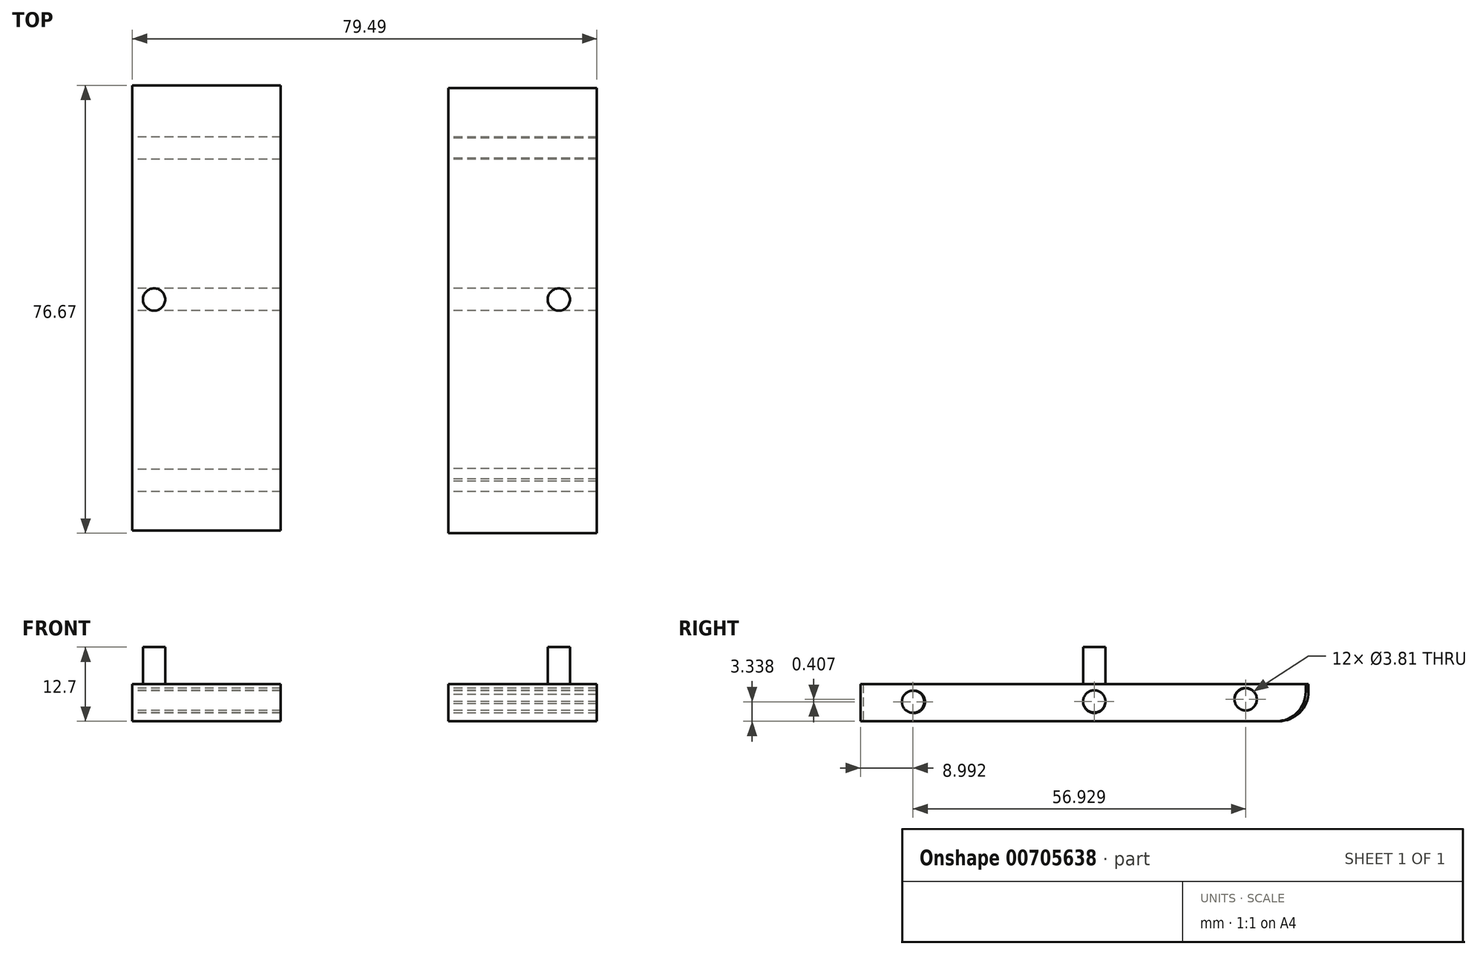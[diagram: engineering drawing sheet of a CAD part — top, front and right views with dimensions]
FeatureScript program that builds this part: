
annotation { "Feature Type Name" : "Feature", "Feature Type Description" : "" }
export const myFeature = defineFeature(function(context is Context, id is Id, definition is map)
    precondition{}
    {
        {
            var Q0;
            Q0=qCreatedBy(makeId("Top.planeOp"),FACE);
            var sketch = newSketch(context, id + "F0", { "sketchPlane" : qUnion([Q0])});
            skLineSegment(sketch, "E0.bottom", {"start": v(-44.7, 36.67) * mm, "end": v(-19.3, 36.67) * mm});
            skLineSegment(sketch, "E0.top", {"start": v(-44.7, -39.53) * mm, "end": v(-19.3, -39.53) * mm});
            skLineSegment(sketch, "E0.left", {"start": v(-44.7, 36.67) * mm, "end": v(-44.7, -39.53) * mm});
            skLineSegment(sketch, "E0.right", {"start": v(-19.3, 36.67) * mm, "end": v(-19.3, -39.53) * mm});
            skLineSegment(sketch, "E1.bottom", {"start": v(9.39, 36.2) * mm, "end": v(34.79, 36.2) * mm});
            skLineSegment(sketch, "E1.top", {"start": v(9.39, -40) * mm, "end": v(34.79, -40) * mm});
            skLineSegment(sketch, "E1.left", {"start": v(9.39, 36.2) * mm, "end": v(9.39, -40) * mm});
            skLineSegment(sketch, "E1.right", {"start": v(34.79, 36.2) * mm, "end": v(34.79, -40) * mm});
            skSolve(sketch);
        }
        {
            var Q0;
            Q0=makeQuery(id+"F0.imprint","IMPRINT",FACE,{"disambiguationData":[TD([[makeQuery(id+"F0.imprint","IMPRINT",EDGE,{"derivedFrom":sQuery(id+"F0.wireOp",EDGE,"E0.bottom")}),-1.0]])]});
            var Q1;
            Q1=makeQuery(id+"F0.imprint","IMPRINT",FACE,{"disambiguationData":[TD([[makeQuery(id+"F0.imprint","IMPRINT",EDGE,{"derivedFrom":sQuery(id+"F0.wireOp",EDGE,"E1.bottom")}),-1.0]])]});
            extrude(context, id + "F1", {"entities" : qUnion([Q0, Q1]), "depth" : 6.35 * mm, "offsetDistance" : 25.4 * mm});
        }
        {
            var Q0;
            Q0=makeQuery(id+"F1.opExtrude","CAP_EDGE",EDGE,{"disambiguationData":[OSD([sQuery(id+"F0.wireOp",EDGE,"E0.bottom")])],"isStart":true});
            var Q1;
            Q1=makeQuery(id+"F1.opExtrude","CAP_EDGE",EDGE,{"disambiguationData":[OSD([sQuery(id+"F0.wireOp",EDGE,"E1.bottom")])],"isStart":true});
            fillet(context, id + "F2", {"entities" : qUnion([Q0, Q1]), "radius" : 5.08 * mm, "tangentPropagation" : true, "allowEdgeOverflow" : false});
        }
        {
            var Q0;
            Q0=makeQuery(id+"F1.opExtrude","SWEPT_FACE",FACE,{"disambiguationData":[OSD([sQuery(id+"F0.wireOp",EDGE,"E0.left")])]});
            var sketch = newSketch(context, id + "F3", { "sketchPlane" : qUnion([Q0])});
            skCircle(sketch, "E2", {"center": v(-25.92, 3.75) * mm, "radius": 1.9 * mm});
            skCircle(sketch, "E3", {"center": v(0, 3.4) * mm, "radius": 1.9 * mm});
            skCircle(sketch, "E4", {"center": v(31, 3.34) * mm, "radius": 1.9 * mm});
            skSolve(sketch);
        }
        {
            var Q0;
            Q0=makeQuery(id+"F3.imprint","IMPRINT",FACE,{"disambiguationData":[TD([[makeQuery(id+"F3.imprint","IMPRINT",EDGE,{"derivedFrom":sQuery(id+"F3.wireOp",EDGE,"E2")}),1.0]])]});
            var Q1;
            Q1=makeQuery(id+"F3.imprint","IMPRINT",FACE,{"disambiguationData":[TD([[makeQuery(id+"F3.imprint","IMPRINT",EDGE,{"derivedFrom":sQuery(id+"F3.wireOp",EDGE,"E3")}),1.0]])]});
            var Q2;
            Q2=makeQuery(id+"F3.imprint","IMPRINT",FACE,{"disambiguationData":[TD([[makeQuery(id+"F3.imprint","IMPRINT",EDGE,{"derivedFrom":sQuery(id+"F3.wireOp",EDGE,"E4")}),1.0]])]});
            extrude(context, id + "F4", {"entities" : qUnion([Q0, Q1, Q2]), "operationType" : NewBodyOperationType.REMOVE, "oppositeDirection" : true, "depth" : 127 * mm, "offsetDistance" : 25.4 * mm});
        }
        {
            var Q0;
            Q0=makeQuery(id+"F1.opExtrude","SWEPT_FACE",FACE,{"disambiguationData":[OSD([sQuery(id+"F0.wireOp",EDGE,"E1.left")])]});
            var sketch = newSketch(context, id + "F5", { "sketchPlane" : qUnion([Q0])});
            skCircle(sketch, "E5", {"center": v(-25.9, 3.79) * mm, "radius": 1.9 * mm});
            skCircle(sketch, "E6", {"center": v(0, 3.32) * mm, "radius": 1.9 * mm});
            skPoint(sketch, "E7.center.orphan", {"position": v(31.07, 3.32) * mm});
            skCircle(sketch, "E8", {"center": v(30.86, 3.32) * mm, "radius": 1.9 * mm});
            skSolve(sketch);
        }
        {
            var Q0;
            Q0=makeQuery(id+"F1.opExtrude","CAP_FACE",FACE,{"disambiguationData":[OSD([sQuery(id+"F0.wireOp",EDGE,"E1.bottom"),sQuery(id+"F0.wireOp",EDGE,"E1.top"),sQuery(id+"F0.wireOp",EDGE,"E1.left"),sQuery(id+"F0.wireOp",EDGE,"E1.right")])],"isStart":false});
            var sketch = newSketch(context, id + "F6", { "sketchPlane" : qUnion([Q0])});
            skCircle(sketch, "E9", {"center": v(28.29, 0) * mm, "radius": 1.9 * mm});
            skCircle(sketch, "E10", {"center": v(-41, 0) * mm, "radius": 1.9 * mm});
            skSolve(sketch);
        }
        {
            var Q0;
            Q0=makeQuery(id+"F6.imprint","IMPRINT",FACE,{"disambiguationData":[TD([[makeQuery(id+"F6.imprint","IMPRINT",EDGE,{"derivedFrom":sQuery(id+"F6.wireOp",EDGE,"E10")}),1.0]])]});
            var Q1;
            Q1=makeQuery(id+"F6.imprint","IMPRINT",FACE,{"disambiguationData":[TD([[makeQuery(id+"F6.imprint","IMPRINT",EDGE,{"derivedFrom":sQuery(id+"F6.wireOp",EDGE,"E9")}),1.0]])]});
            extrude(context, id + "F7", {"entities" : qUnion([Q0, Q1]), "depth" : 6.35 * mm, "offsetDistance" : 25.4 * mm});
        }
        {
            var Q0;
            Q0=makeQuery(id+"F5.imprint","IMPRINT",FACE,{"disambiguationData":[TD([[makeQuery(id+"F5.imprint","IMPRINT",EDGE,{"derivedFrom":sQuery(id+"F5.wireOp",EDGE,"E5")}),1.0]])]});
            var Q1;
            Q1=makeQuery(id+"F5.imprint","IMPRINT",FACE,{"disambiguationData":[TD([[makeQuery(id+"F5.imprint","IMPRINT",EDGE,{"derivedFrom":sQuery(id+"F5.wireOp",EDGE,"E6")}),1.0]])]});
            var Q2;
            Q2=makeQuery(id+"F5.imprint","IMPRINT",FACE,{"disambiguationData":[TD([[makeQuery(id+"F5.imprint","IMPRINT",EDGE,{"derivedFrom":sQuery(id+"F5.wireOp",EDGE,"E8")}),1.0]])]});
            var Q3;
            Q3=sQuery(id+"F5.wireOp",EDGE,"E6");
            var Q4;
            Q4=sQuery(id+"F5.wireOp",EDGE,"E8");
            var Q5;
            Q5=sQuery(id+"F5.wireOp",EDGE,"E5");
            extrude(context, id + "F8", {"entities" : qUnion([Q0, Q1, Q2]), "operationType" : NewBodyOperationType.REMOVE, "surfaceEntities" : qUnion([Q3, Q4, Q5]), "oppositeDirection" : true, "depth" : 101.6 * mm, "offsetDistance" : 25.4 * mm});
        }
    });
